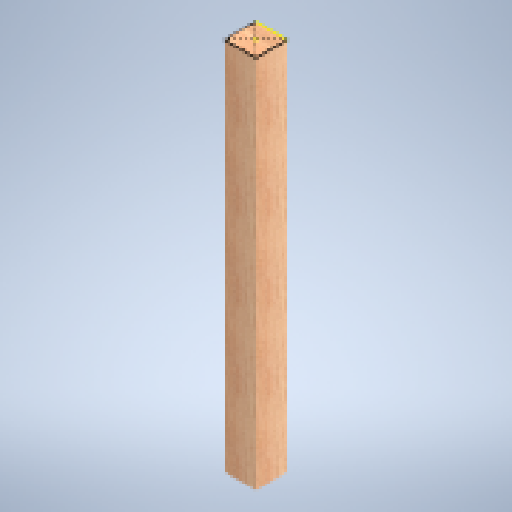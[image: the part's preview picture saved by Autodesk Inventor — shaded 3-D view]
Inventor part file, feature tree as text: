
AUTODESK INVENTOR PART (.ipt)
format: ipt  version: 2025 (Build 290162000, 162)  size: 333,312 bytes
history: native  units: in
note: dims shown in document units (in); Inventor stores cm internally (conversion verified against a paired STEP export)
features: sketch x2, extrude x1
ambient origin geometry x8: Origin, YZ Plane, XZ Plane, XY Plane, X Axis, Y Axis, Z Axis, Center Point
bodies: Solid1 (feature_tree)
feature tree (3):
  extrude  "Extrusion1"  Depth=4.0in
  sketch  "Sketch2"  dims[d2=40.0in d3=0.0in d4=0.5in d5=0.0344in d6=0.5in d7=0.0344in]
  sketch  "Sketch1"  dims[d0=4.0in d1=4.0in]
